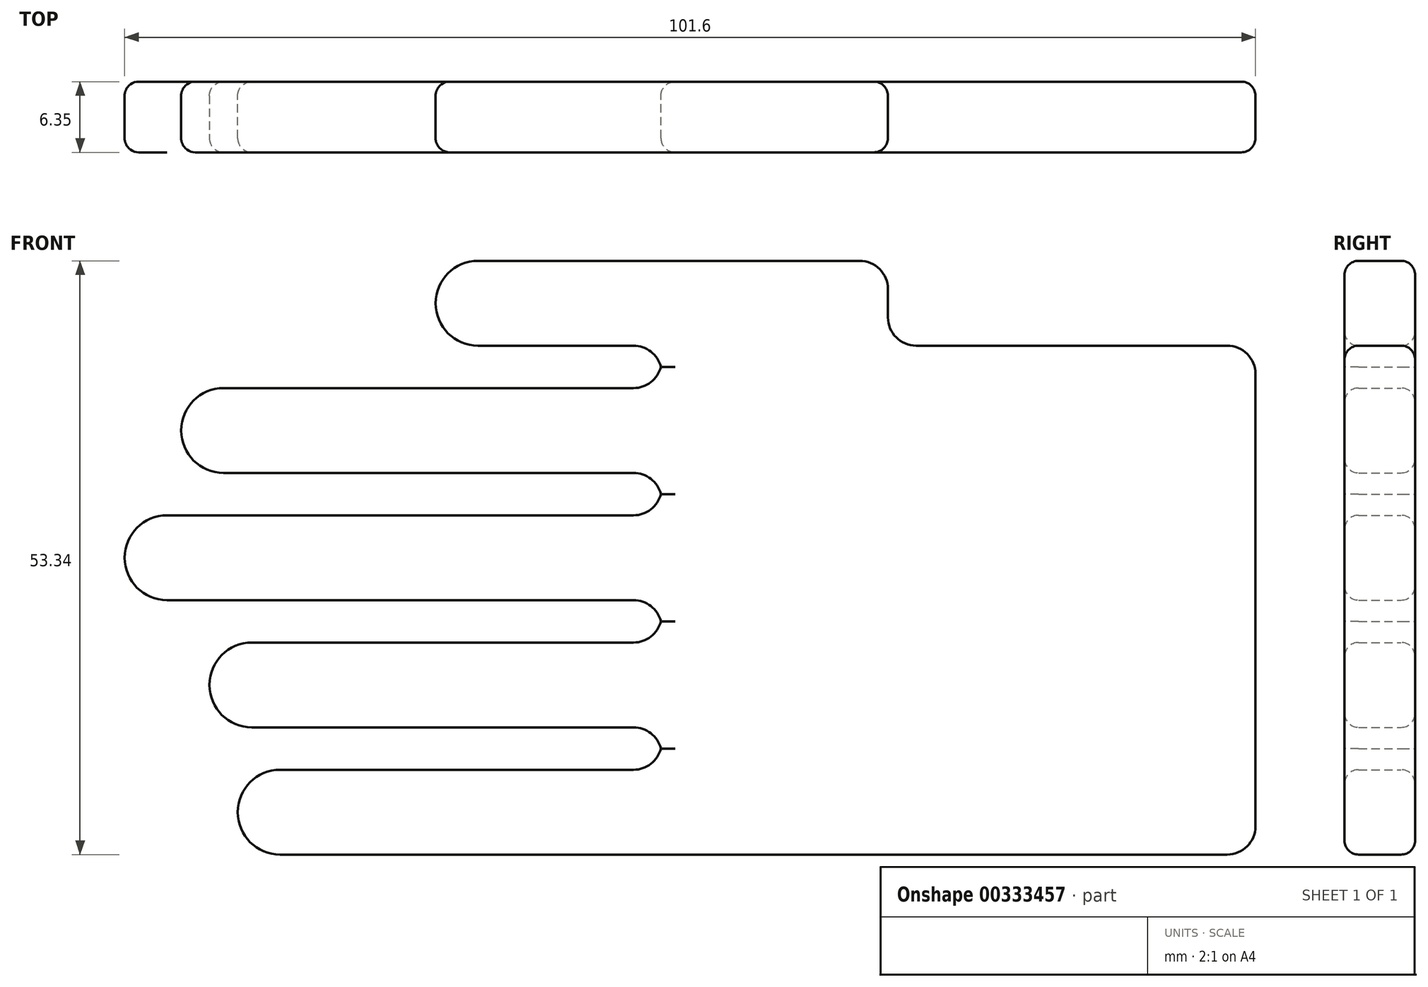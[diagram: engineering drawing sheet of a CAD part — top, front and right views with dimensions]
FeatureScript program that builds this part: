
annotation { "Feature Type Name" : "Feature", "Feature Type Description" : "" }
export const myFeature = defineFeature(function(context is Context, id is Id, definition is map)
    precondition{}
    {
        {
            var Q0;
            Q0=qCreatedBy(makeId("Front.planeOp"),FACE);
            var sketch = newSketch(context, id + "F0", { "sketchPlane" : qUnion([Q0])});
            skLineSegment(sketch, "E0.bottom", {"start": v(-30.61, 28.27) * mm, "end": v(22.73, 28.27) * mm});
            skLineSegment(sketch, "E0.top", {"start": v(-30.61, -17.45) * mm, "end": v(22.73, -17.45) * mm});
            skLineSegment(sketch, "E0.left", {"start": v(-30.61, 28.27) * mm, "end": v(-30.61, -17.45) * mm});
            skLineSegment(sketch, "E0.right", {"start": v(22.73, 28.27) * mm, "end": v(22.73, -17.45) * mm});
            skLineSegment(sketch, "E1.bottom", {"start": v(-10.3, 28.27) * mm, "end": v(-50.93, 28.27) * mm});
            skLineSegment(sketch, "E1.top", {"start": v(-10.3, 35.89) * mm, "end": v(-50.93, 35.89) * mm});
            skLineSegment(sketch, "E1.left", {"start": v(-10.3, 28.27) * mm, "end": v(-10.3, 35.89) * mm});
            skLineSegment(sketch, "E1.right", {"start": v(-50.93, 28.27) * mm, "end": v(-50.93, 35.89) * mm});
            skLineSegment(sketch, "E2.bottom", {"start": v(-30.61, 24.46) * mm, "end": v(-73.8, 24.46) * mm});
            skLineSegment(sketch, "E2.top", {"start": v(-30.61, 16.84) * mm, "end": v(-73.8, 16.84) * mm});
            skLineSegment(sketch, "E2.left", {"start": v(-30.61, 24.46) * mm, "end": v(-30.61, 16.84) * mm});
            skLineSegment(sketch, "E2.right", {"start": v(-73.8, 24.46) * mm, "end": v(-73.8, 16.84) * mm});
            skLineSegment(sketch, "E3.bottom", {"start": v(-30.61, 13.03) * mm, "end": v(-78.87, 13.03) * mm});
            skLineSegment(sketch, "E3.top", {"start": v(-30.61, 5.4) * mm, "end": v(-78.87, 5.4) * mm});
            skLineSegment(sketch, "E3.left", {"start": v(-30.61, 13.03) * mm, "end": v(-30.61, 5.4) * mm});
            skLineSegment(sketch, "E3.right", {"start": v(-78.87, 13.03) * mm, "end": v(-78.87, 5.4) * mm});
            skLineSegment(sketch, "E4.bottom", {"start": v(-30.61, 1.6) * mm, "end": v(-71.25, 1.6) * mm});
            skLineSegment(sketch, "E4.top", {"start": v(-30.61, -6.02) * mm, "end": v(-71.25, -6.02) * mm});
            skLineSegment(sketch, "E4.left", {"start": v(-30.61, 1.6) * mm, "end": v(-30.61, -6.02) * mm});
            skLineSegment(sketch, "E4.right", {"start": v(-71.25, 1.6) * mm, "end": v(-71.25, -6.02) * mm});
            skLineSegment(sketch, "E5.bottom", {"start": v(-30.61, -9.83) * mm, "end": v(-68.71, -9.83) * mm});
            skLineSegment(sketch, "E5.top", {"start": v(-30.61, -17.45) * mm, "end": v(-68.71, -17.45) * mm});
            skLineSegment(sketch, "E5.left", {"start": v(-30.61, -9.83) * mm, "end": v(-30.61, -17.45) * mm});
            skLineSegment(sketch, "E5.right", {"start": v(-68.71, -9.83) * mm, "end": v(-68.71, -17.45) * mm});
            skSolve(sketch);
        }
        {
            var Q0;
            Q0=makeQuery(id+"F0.imprint","IMPRINT",FACE,{"disambiguationData":[TD([[makeQuery(id+"F0.imprint","IMPRINT",EDGE,{"derivedFrom":sQuery(id+"F0.wireOp",EDGE,"E1.top")}),1.0]])]});
            var Q1;
            Q1=makeQuery(id+"F0.imprint","IMPRINT",FACE,{"disambiguationData":[TD([[makeQuery(id+"F0.imprint","IMPRINT",EDGE,{"derivedFrom":sQuery(id+"F0.wireOp",EDGE,"E2.bottom")}),1.0]])]});
            var Q2;
            Q2=makeQuery(id+"F0.imprint","IMPRINT",FACE,{"disambiguationData":[TD([[makeQuery(id+"F0.imprint","IMPRINT",EDGE,{"derivedFrom":sQuery(id+"F0.wireOp",EDGE,"E3.bottom")}),1.0]])]});
            var Q3;
            Q3=makeQuery(id+"F0.imprint","IMPRINT",FACE,{"disambiguationData":[TD([[makeQuery(id+"F0.imprint","IMPRINT",EDGE,{"derivedFrom":sQuery(id+"F0.wireOp",EDGE,"E4.bottom")}),1.0]])]});
            var Q4;
            Q4=makeQuery(id+"F0.imprint","IMPRINT",FACE,{"disambiguationData":[TD([[makeQuery(id+"F0.imprint","IMPRINT",EDGE,{"derivedFrom":sQuery(id+"F0.wireOp",EDGE,"E5.bottom")}),1.0]])]});
            var Q5;
            {var subQ2=sQuery(id+"F0.wireOp",EDGE,"E0.bottom");Q5=makeQuery(id+"F0.imprint","IMPRINT",FACE,{"disambiguationData":[TD([[makeQuery(id+"F0.imprint","IMPRINT",EDGE,{"derivedFrom":subQ2}),-1.0]])]});}
            extrude(context, id + "F1", {"entities" : qUnion([Q0, Q1, Q2, Q3, Q4, Q5]), "depth" : 6.35 * mm});
        }
        {
            var Q0;
            Q0=makeQuery(id+"F1.opExtrude","SWEPT_EDGE",EDGE,{"disambiguationData":[OSD([sQuery(id+"F0.wireOp",EDGE,"E2.bottom"),sQuery(id+"F0.wireOp",EDGE,"E2.right")])]});
            var Q1;
            Q1=makeQuery(id+"F1.opExtrude","SWEPT_EDGE",EDGE,{"disambiguationData":[OSD([sQuery(id+"F0.wireOp",EDGE,"E2.top"),sQuery(id+"F0.wireOp",EDGE,"E2.right")])]});
            var Q2;
            Q2=makeQuery(id+"F1.opExtrude","SWEPT_EDGE",EDGE,{"disambiguationData":[OSD([sQuery(id+"F0.wireOp",EDGE,"E3.top"),sQuery(id+"F0.wireOp",EDGE,"E3.right")])]});
            var Q3;
            Q3=makeQuery(id+"F1.opExtrude","SWEPT_EDGE",EDGE,{"disambiguationData":[OSD([sQuery(id+"F0.wireOp",EDGE,"E3.bottom"),sQuery(id+"F0.wireOp",EDGE,"E3.right")])]});
            var Q4;
            Q4=makeQuery(id+"F1.opExtrude","SWEPT_EDGE",EDGE,{"disambiguationData":[OSD([sQuery(id+"F0.wireOp",EDGE,"E4.top"),sQuery(id+"F0.wireOp",EDGE,"E4.right")])]});
            var Q5;
            Q5=makeQuery(id+"F1.opExtrude","SWEPT_EDGE",EDGE,{"disambiguationData":[OSD([sQuery(id+"F0.wireOp",EDGE,"E4.bottom"),sQuery(id+"F0.wireOp",EDGE,"E4.right")])]});
            var Q6;
            Q6=makeQuery(id+"F1.opExtrude","SWEPT_EDGE",EDGE,{"disambiguationData":[OSD([sQuery(id+"F0.wireOp",EDGE,"E5.bottom"),sQuery(id+"F0.wireOp",EDGE,"E5.right")])]});
            var Q7;
            Q7=makeQuery(id+"F1.opExtrude","SWEPT_EDGE",EDGE,{"disambiguationData":[OSD([sQuery(id+"F0.wireOp",EDGE,"E5.top"),sQuery(id+"F0.wireOp",EDGE,"E5.right")])]});
            var Q8;
            Q8=makeQuery(id+"F1.opExtrude","SWEPT_EDGE",EDGE,{"disambiguationData":[OSD([sQuery(id+"F0.wireOp",EDGE,"E1.top"),sQuery(id+"F0.wireOp",EDGE,"E1.right")])]});
            var Q9;
            Q9=makeQuery(id+"F1.opExtrude","SWEPT_EDGE",EDGE,{"disambiguationData":[OSD([sQuery(id+"F0.wireOp",EDGE,"E1.bottom"),sQuery(id+"F0.wireOp",EDGE,"E1.right")])]});
            fillet(context, id + "F2", {"entities" : qUnion([Q0, Q1, Q2, Q3, Q4, Q5, Q6, Q7, Q8, Q9]), "radius" : 3.8 * mm, "tangentPropagation" : true, "allowEdgeOverflow" : false});
        }
        {
            var Q0;
            Q0=makeQuery(id+"F1.opExtrude","SWEPT_EDGE",EDGE,{"disambiguationData":[OSD([sQuery(id+"F0.wireOp",EDGE,"E1.top"),sQuery(id+"F0.wireOp",EDGE,"E1.left")])]});
            var Q1;
            Q1=makeQuery(id+"F1.opExtrude","SWEPT_EDGE",EDGE,{"disambiguationData":[OSD([sQuery(id+"F0.wireOp",EDGE,"E0.bottom"),sQuery(id+"F0.wireOp",EDGE,"E1.bottom"),sQuery(id+"F0.wireOp",EDGE,"E1.left")])]});
            var Q2;
            Q2=makeQuery(id+"F1.opExtrude","SWEPT_EDGE",EDGE,{"disambiguationData":[OSD([sQuery(id+"F0.wireOp",EDGE,"E0.bottom"),sQuery(id+"F0.wireOp",EDGE,"E0.right")])]});
            var Q3;
            Q3=makeQuery(id+"F1.opExtrude","SWEPT_EDGE",EDGE,{"disambiguationData":[OSD([sQuery(id+"F0.wireOp",EDGE,"E0.top"),sQuery(id+"F0.wireOp",EDGE,"E0.right")])]});
            var Q4;
            Q4=makeQuery(id+"F1.opExtrude","SWEPT_EDGE",EDGE,{"disambiguationData":[OSD([sQuery(id+"F0.wireOp",EDGE,"E0.left"),sQuery(id+"F0.wireOp",EDGE,"E1.bottom")])]});
            var Q5;
            Q5=makeQuery(id+"F1.opExtrude","SWEPT_EDGE",EDGE,{"disambiguationData":[OSD([sQuery(id+"F0.wireOp",EDGE,"E0.left"),sQuery(id+"F0.wireOp",EDGE,"E2.top"),sQuery(id+"F0.wireOp",EDGE,"E2.left")])]});
            var Q6;
            Q6=makeQuery(id+"F1.opExtrude","SWEPT_EDGE",EDGE,{"disambiguationData":[OSD([sQuery(id+"F0.wireOp",EDGE,"E0.left"),sQuery(id+"F0.wireOp",EDGE,"E3.top"),sQuery(id+"F0.wireOp",EDGE,"E3.left")])]});
            var Q7;
            Q7=makeQuery(id+"F1.opExtrude","SWEPT_EDGE",EDGE,{"disambiguationData":[OSD([sQuery(id+"F0.wireOp",EDGE,"E0.left"),sQuery(id+"F0.wireOp",EDGE,"E4.top"),sQuery(id+"F0.wireOp",EDGE,"E4.left")])]});
            var Q8;
            Q8=makeQuery(id+"F1.opExtrude","SWEPT_EDGE",EDGE,{"disambiguationData":[OSD([sQuery(id+"F0.wireOp",EDGE,"E0.left"),sQuery(id+"F0.wireOp",EDGE,"E2.bottom"),sQuery(id+"F0.wireOp",EDGE,"E2.left")])]});
            var Q9;
            Q9=makeQuery(id+"F1.opExtrude","SWEPT_EDGE",EDGE,{"disambiguationData":[OSD([sQuery(id+"F0.wireOp",EDGE,"E0.left"),sQuery(id+"F0.wireOp",EDGE,"E3.bottom"),sQuery(id+"F0.wireOp",EDGE,"E3.left")])]});
            var Q10;
            Q10=makeQuery(id+"F1.opExtrude","SWEPT_EDGE",EDGE,{"disambiguationData":[OSD([sQuery(id+"F0.wireOp",EDGE,"E0.left"),sQuery(id+"F0.wireOp",EDGE,"E4.bottom"),sQuery(id+"F0.wireOp",EDGE,"E4.left")])]});
            var Q11;
            Q11=makeQuery(id+"F1.opExtrude","SWEPT_EDGE",EDGE,{"disambiguationData":[OSD([sQuery(id+"F0.wireOp",EDGE,"E0.left"),sQuery(id+"F0.wireOp",EDGE,"E5.bottom"),sQuery(id+"F0.wireOp",EDGE,"E5.left")])]});
            fillet(context, id + "F3", {"entities" : qUnion([Q0, Q1, Q2, Q3, Q4, Q5, Q6, Q7, Q8, Q9, Q10, Q11]), "radius" : 2.54 * mm, "tangentPropagation" : true, "allowEdgeOverflow" : false});
        }
        {
            var Q0;
            Q0=makeQuery(id+"F1.opExtrude","CAP_EDGE",EDGE,{"disambiguationData":[OSD([sQuery(id+"F0.wireOp",EDGE,"E1.bottom")])],"isStart":false});
            var Q1;
            Q1=makeQuery(id+"F1.opExtrude","CAP_EDGE",EDGE,{"disambiguationData":[OSD([sQuery(id+"F0.wireOp",EDGE,"E1.bottom")])],"isStart":true});
            var Q2;
            Q2=makeQuery(id+"F1.opExtrude","CAP_EDGE",EDGE,{"disambiguationData":[OSD([sQuery(id+"F0.wireOp",EDGE,"E2.bottom")])],"isStart":false});
            var Q3;
            Q3=makeQuery(id+"F1.opExtrude","CAP_EDGE",EDGE,{"disambiguationData":[OSD([sQuery(id+"F0.wireOp",EDGE,"E3.bottom")])],"isStart":false});
            var Q4;
            Q4=makeQuery(id+"F1.opExtrude","CAP_EDGE",EDGE,{"disambiguationData":[OSD([sQuery(id+"F0.wireOp",EDGE,"E4.top")])],"isStart":true});
            var Q5;
            Q5=makeQuery(id+"F1.opExtrude","CAP_EDGE",EDGE,{"disambiguationData":[OSD([sQuery(id+"F0.wireOp",EDGE,"E4.bottom")])],"isStart":true});
            var Q6;
            Q6=makeQuery(id+"F1.opExtrude","CAP_EDGE",EDGE,{"disambiguationData":[OSD([sQuery(id+"F0.wireOp",EDGE,"E3.bottom")])],"isStart":true});
            var Q7;
            Q7=makeQuery(id+"F1.opExtrude","CAP_EDGE",EDGE,{"disambiguationData":[OSD([sQuery(id+"F0.wireOp",EDGE,"E2.bottom")])],"isStart":true});
            var Q8;
            Q8=makeQuery(id+"F1.opExtrude","CAP_EDGE",EDGE,{"disambiguationData":[OSD([sQuery(id+"F0.wireOp",EDGE,"E4.top")])],"isStart":false});
            fillet(context, id + "F4", {"entities" : qUnion([Q0, Q1, Q2, Q3, Q4, Q5, Q6, Q7, Q8]), "radius" : 1.27 * mm, "tangentPropagation" : true, "allowEdgeOverflow" : false});
        }
    });
